# Revit family: Sink-Kitchen-DXV-ETRE-D21180SB3320.415
name_source: partatom
category: Plumbing Fixtures
units: mm (PartAtom-declared; Revit-internal decimal feet)

## family parameters
Always vertical = No
Cut with Voids When Loaded = No
OmniClass Number = 23.45.05.14.14
OmniClass Title = Sinks/Lavatories
Part Type = Normal
Room Calculation Point = No
Round Connector Dimension = Use Radius
Shared = Yes
Work Plane-Based = Yes

## types (1)
- D21180SB3320.415
    7301839-201 Drain with Strainer = Yes
    7302390-401 Sink Rack = No
    Assembly Code = D2010410
    Basin Shape = Rectangle
    Bowl Height = 8 3/4"
    Bowl Length = 31 3/16"
    Bowl Width = 18 7/16"
    CW Connection = Yes
    CWFU = 1.5
    Cold Water Connection Diameter = 1/2"
    Cold Water Connection Height = 20"
    Cold Water Connection Radius = 1/4"
    Cold Water Connection Width = 4"
    Compliance Certifications = Meets or Exceeds ASME A112.19.2 / CSA B45.1
    Default Elevation = 34"
    Description = Etre 33 in. Apron Kitchen Sink with Offset Drain
    Finish = Fire Clay-DXV-415-White
    HW Connection = Yes
    HWFU = 1.5
    Height = 10"
    Hot Water Connection Diameter = 1/2"
    Hot Water Connection Height = 20"
    Hot Water Connection Radius = 1/4"
    Hot Water Connection Width = 4"
    Installation Type = Undermount or flush mount
    Length = 32 3/4"
    Manufacturer = DXV
    Material = Fire Clay-DXV-415-White
    Model = D21180SB3320.415
    Product Documentation Link = https://americanstandard.box.com
    Product Page URL = https://www.dxv.com
    Type Comments = 36" (914 mm) cabinet required
    URL = https://www.dxv.com
    Vent Connection = No
    WFU = 2
    Warranty Information = 5-year limited warranty on sink; 1 year on accessories
    Waste Connection = Yes
    Waste Connection Diameter = 1 1/4"
    Waste Connection Height = 18"
    Waste Connection Radius = 5/8"
    Width = 20"

## geometry (parser evidence)
native form markers: Sweep x5
no freeform markers — native parametric forms only
